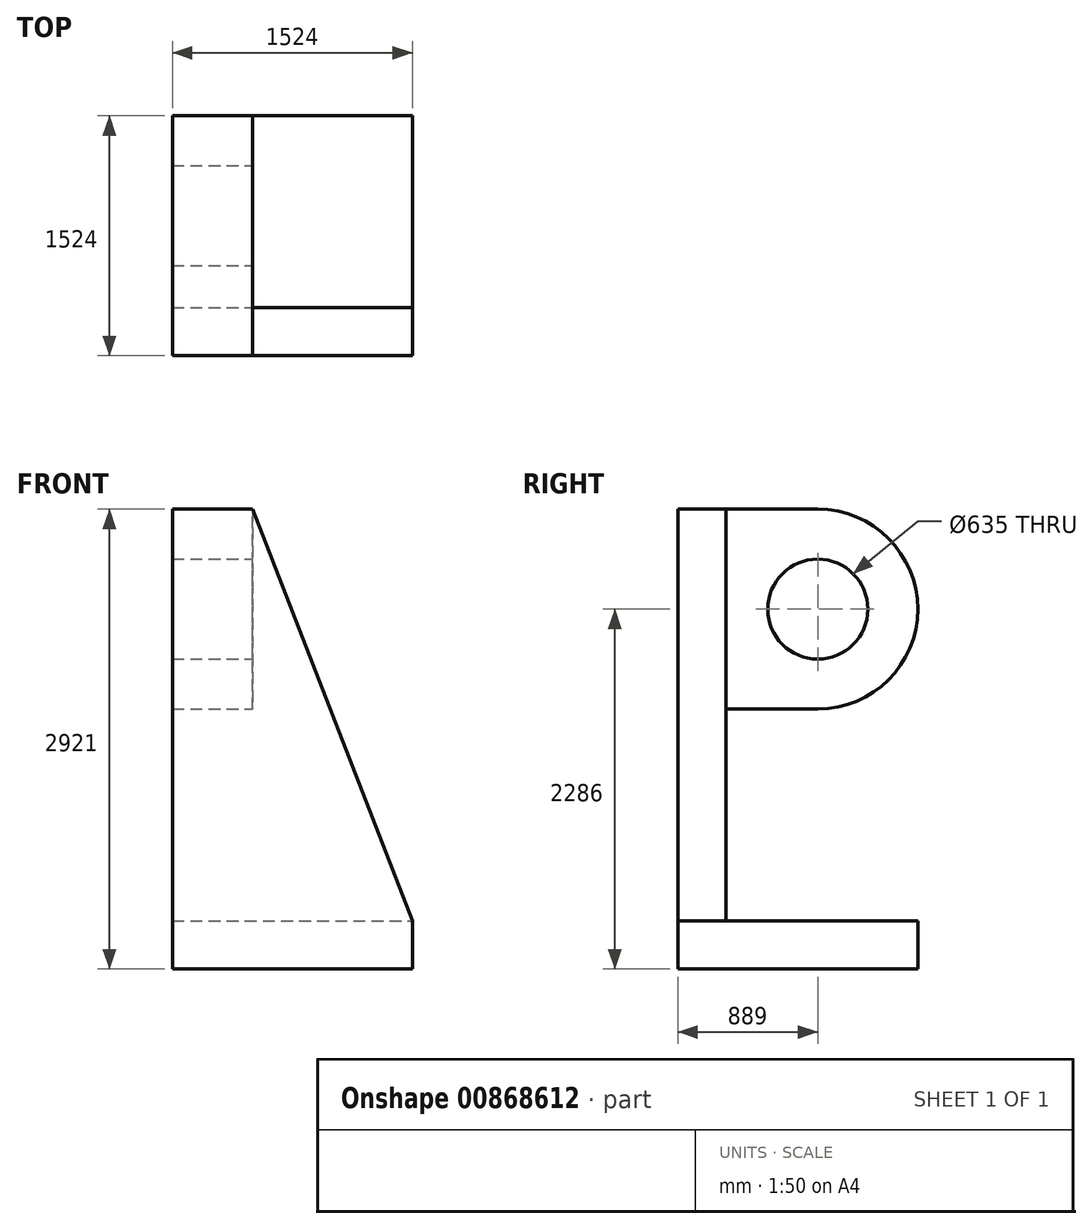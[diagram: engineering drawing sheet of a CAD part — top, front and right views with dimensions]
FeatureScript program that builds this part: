
annotation { "Feature Type Name" : "Feature", "Feature Type Description" : "" }
export const myFeature = defineFeature(function(context is Context, id is Id, definition is map)
    precondition{}
    {
        {
            var Q0;
            Q0=qCreatedBy(makeId("Top.planeOp"),FACE);
            var sketch = newSketch(context, id + "F0", { "sketchPlane" : qUnion([Q0])});
            skLineSegment(sketch, "E0", {"start": v(0, 0) * mm, "end": v(1524, 0) * mm});
            skLineSegment(sketch, "E1", {"start": v(1524, 0) * mm, "end": v(1524, -1524) * mm});
            skLineSegment(sketch, "E2", {"start": v(1524, -1524) * mm, "end": v(0, -1524) * mm});
            skLineSegment(sketch, "E3", {"start": v(0, -1524) * mm, "end": v(0, 0) * mm});
            skSolve(sketch);
        }
        {
            var Q0;
            Q0=makeQuery(id+"F0.imprint","IMPRINT",FACE,{"disambiguationData":[TD([[makeQuery(id+"F0.imprint","IMPRINT",EDGE,{"derivedFrom":sQuery(id+"F0.wireOp",EDGE,"E0")}),-1.0]])]});
            extrude(context, id + "F1", {"entities" : qUnion([Q0]), "depth" : 304.8 * mm, "offsetDistance" : 25.4 * mm});
        }
        {
            var Q0;
            Q0=makeQuery(id+"F1.opExtrude","CAP_FACE",FACE,{"disambiguationData":[OSD([sQuery(id+"F0.wireOp",EDGE,"E0"),sQuery(id+"F0.wireOp",EDGE,"E1"),sQuery(id+"F0.wireOp",EDGE,"E2"),sQuery(id+"F0.wireOp",EDGE,"E3")])],"isStart":false});
            var sketch = newSketch(context, id + "F2", { "sketchPlane" : qUnion([Q0])});
            skLineSegment(sketch, "E4", {"start": v(0, -1524) * mm, "end": v(0, -1219.2) * mm});
            skLineSegment(sketch, "E5", {"start": v(0, -1219.2) * mm, "end": v(1524, -1219.2) * mm});
            skLineSegment(sketch, "E6", {"start": v(1524, -1219.2) * mm, "end": v(1524, -1524) * mm});
            skLineSegment(sketch, "E7", {"start": v(1524, -1524) * mm, "end": v(0, -1524) * mm});
            skSolve(sketch);
        }
        {
            var Q0;
            Q0=makeQuery(id+"F2.imprint","IMPRINT",FACE,{"disambiguationData":[TD([[makeQuery(id+"F2.imprint","IMPRINT",EDGE,{"derivedFrom":sQuery(id+"F2.wireOp",EDGE,"E4")}),-1.0]])]});
            extrude(context, id + "F3", {"entities" : qUnion([Q0]), "operationType" : NewBodyOperationType.ADD, "depth" : 2616.2 * mm, "offsetDistance" : 25.4 * mm});
        }
        {
            var Q0;
            Q0=makeQuery(id+"F3.opExtrude","SWEPT_FACE",FACE,{"disambiguationData":[OSD([sQuery(id+"F2.wireOp",EDGE,"E5")])]});
            var sketch = newSketch(context, id + "F4", { "sketchPlane" : qUnion([Q0])});
            skLineSegment(sketch, "E8.bottom", {"start": v(0, 2921) * mm, "end": v(-508, 2921) * mm});
            skLineSegment(sketch, "E8.top", {"start": v(0, 1651) * mm, "end": v(-508, 1651) * mm});
            skLineSegment(sketch, "E8.left", {"start": v(0, 2921) * mm, "end": v(0, 1651) * mm});
            skLineSegment(sketch, "E8.right", {"start": v(-508, 2921) * mm, "end": v(-508, 1651) * mm});
            skSolve(sketch);
        }
        {
            var Q0;
            Q0=makeQuery(id+"F4.imprint","IMPRINT",FACE,{"disambiguationData":[TD([[makeQuery(id+"F4.imprint","IMPRINT",EDGE,{"derivedFrom":sQuery(id+"F4.wireOp",EDGE,"E8.bottom")}),1.0]])]});
            extrude(context, id + "F5", {"entities" : qUnion([Q0]), "operationType" : NewBodyOperationType.ADD, "depth" : 584.2 * mm, "offsetDistance" : 25.4 * mm});
        }
        {
            var Q0;
            Q0=makeQuery(id+"F5.opExtrude","SWEPT_FACE",FACE,{"disambiguationData":[OSD([sQuery(id+"F4.wireOp",EDGE,"E8.right")])]});
            var sketch = newSketch(context, id + "F6", { "sketchPlane" : qUnion([Q0])});
            skCircle(sketch, "E9", {"center": v(-635, 2286) * mm, "radius": 635 * mm});
            skSolve(sketch);
        }
        {
            var Q0;
            {var subQ1=sQuery(id+"F4.wireOp",EDGE,"E8.right");var subQ2=makeQuery(id+"F5.opExtrude","CAP_EDGE",EDGE,{"disambiguationData":[OSD([subQ1])],"isStart":false});Q0=makeQuery(id+"F6.imprint","IMPRINT",FACE,{"disambiguationData":[TD([[makeQuery(id+"F6.imprint","IMPRINT",EDGE,{"derivedFrom":subQ2}),1.0]])]});}
            extrude(context, id + "F7", {"entities" : qUnion([Q0]), "operationType" : NewBodyOperationType.ADD, "oppositeDirection" : true, "depth" : 508 * mm, "offsetDistance" : 25.4 * mm});
        }
        {
            var Q0;
            {var subQ0=sQuery(id+"F4.wireOp",EDGE,"E8.right");Q0=makeQuery(id+"F7.boolean.opBoolean","MERGE",FACE,{"derivedFrom":[makeQuery(id+"F5.opExtrude","SWEPT_FACE",FACE,{"disambiguationData":[OSD([subQ0])]}),makeQuery(id+"F7.opExtrude","CAP_FACE",FACE,{"disambiguationData":[OSD([subQ0,sQuery(id+"F6.wireOp",EDGE,"E9")])],"isStart":true})]});}
            var sketch = newSketch(context, id + "F8", { "sketchPlane" : qUnion([Q0])});
            skCircle(sketch, "E10", {"center": v(-635, 2286) * mm, "radius": 317.5 * mm});
            skSolve(sketch);
        }
        {
            var Q0;
            Q0=makeQuery(id+"F8.imprint","IMPRINT",FACE,{"disambiguationData":[TD([[makeQuery(id+"F8.imprint","IMPRINT",EDGE,{"derivedFrom":sQuery(id+"F8.wireOp",EDGE,"E10")}),1.0]])]});
            extrude(context, id + "F9", {"entities" : qUnion([Q0]), "operationType" : NewBodyOperationType.REMOVE, "oppositeDirection" : true, "depth" : 508 * mm, "offsetDistance" : 25.4 * mm});
        }
        {
            var Q0;
            Q0=makeQuery(id+"F3.opExtrude","SWEPT_FACE",FACE,{"disambiguationData":[OSD([sQuery(id+"F2.wireOp",EDGE,"E5")])]});
            var sketch = newSketch(context, id + "F10", { "sketchPlane" : qUnion([Q0])});
            skLineSegment(sketch, "E11", {"start": v(-508, 2921) * mm, "end": v(-1524, 304.8) * mm});
            skSolve(sketch);
        }
        {
            var Q0;
            Q0=makeQuery(id+"F10.imprint","IMPRINT",FACE,{"disambiguationData":[TD([[makeQuery(id+"F10.imprint","IMPRINT",EDGE,{"derivedFrom":sQuery(id+"F10.wireOp",EDGE,"E11")}),-1.0]])]});
            extrude(context, id + "F11", {"entities" : qUnion([Q0]), "operationType" : NewBodyOperationType.REMOVE, "oppositeDirection" : true, "depth" : 304.8 * mm, "offsetDistance" : 25.4 * mm});
        }
    });
